# Revit family: KS Polar plus, DS 20, Ø108-114,3
name_source: partatom
category: Allgemeines Modell
revit_build: Autodesk Revit 2018 (Build: 20190510_1515(x64)
units: mm (PartAtom-declared; Revit-internal decimal feet)

## family parameters
Arbeitsebenenbasiert = Ja
Beim Laden mit Abzugskörper schneiden = Nein
Bemaßung runder Anschluss = Durchmesser verwenden
Gemeinsam genutzt = Ja
Immer vertikal = Nein
Kann Basisbauteil für Bewehrung sein = Nein
Raumberechnungspunkt = Nein
Teiletyp = Normal

## types (2) — shared parameters
A = 46 mm  [stored 0.150919 ft]
Anschluss = M10/M12
Anschlußhöhe = 45 mm
B = 226 mm
Baustoffklasse = B2
Breite = 226 mm
DF1 = 29 mm
DF2 = 34 mm
DS = 20 mm  [stored 0.0656168 ft]
DVS = 18 mm  [stored 0.0590551 ft]
Dichte Kern = 145 kg/m³
Dmax = 115 mm
Dmin = 108 mm
Dämmkörper = AC/PU
Dämmstärke = 20 mm  [stored 0.0656168 ft]
Fabrikat = MEFA
Firma = MEFA Befestigungs- und Montagesysteme GmbH
HGA = 22 mm  [stored 0.0721785 ft]
Kurztext1 = Kälteschelle Polar Plus
L = 51 mm
MB = 35 mm  [stored 0.114829 ft]
MD = 4 mm  [stored 0.0131234 ft]
Material = Stahl
Materialname = S235
Mengeneinheit = St
Oberflaeche = galvanisch verzinkt
Rohrschellentyp = Maxima PSM
S = 197 mm
Schalenlänge = 51 mm
Vorgabe-Ansicht = 1219 mm
Wasserdampfdiffusionswiderstand = 7000 µ
Wärmeleitfähigkeit = 0.031 W/mK
max. Temperaturbeständigkeit = 105 °C
mittl. Nenndruckfestigkeit Kern = 1,9 N/mm²
stat. Belastung Kern = 0,38 N/mm²
vpe = 10 St

## per-type parameters (varying)
| type | AB | Artikelnummer | D | D0 | EAN | Gewicht | Gewicht pro Bauteil | H | Kurztext2 | R | RM | Rohraußendurchmesser Stahl | max. zul. Last |
| Kälteschelle Polar plus, DS 20, M10/M12, Ø108 | 0 mm  [stored 0 ft] | 74621080 | 108 mm | 148 mm | 4250928442659 | 0.84 kg | 0.84 kg | 178 mm | 108 mm Iso 20 x 51 mm M10/M12 | 74 mm | 78 mm | 108 mm | 1.93 kN |
| Kälteschelle Polar plus, DS 20, M10/M12, Ø114,3 | 6 mm  [stored 0.019685 ft] | 74621140 | 114 mm | 154 mm | 4250928442666 | 0.83 kg | 0.83 kg | 184 mm | 114,3 mm Iso 20 x 51 mm M10/M12 | 77 mm | 81 mm | 114,3 mm | 2.05 kN |

note: [stored X ft] marks values corroborated as IEEE doubles in the binary element streams (Revit-internal decimal feet)

## geometry (parser evidence)
native form markers: Sweep x4
no freeform markers — native parametric forms only
